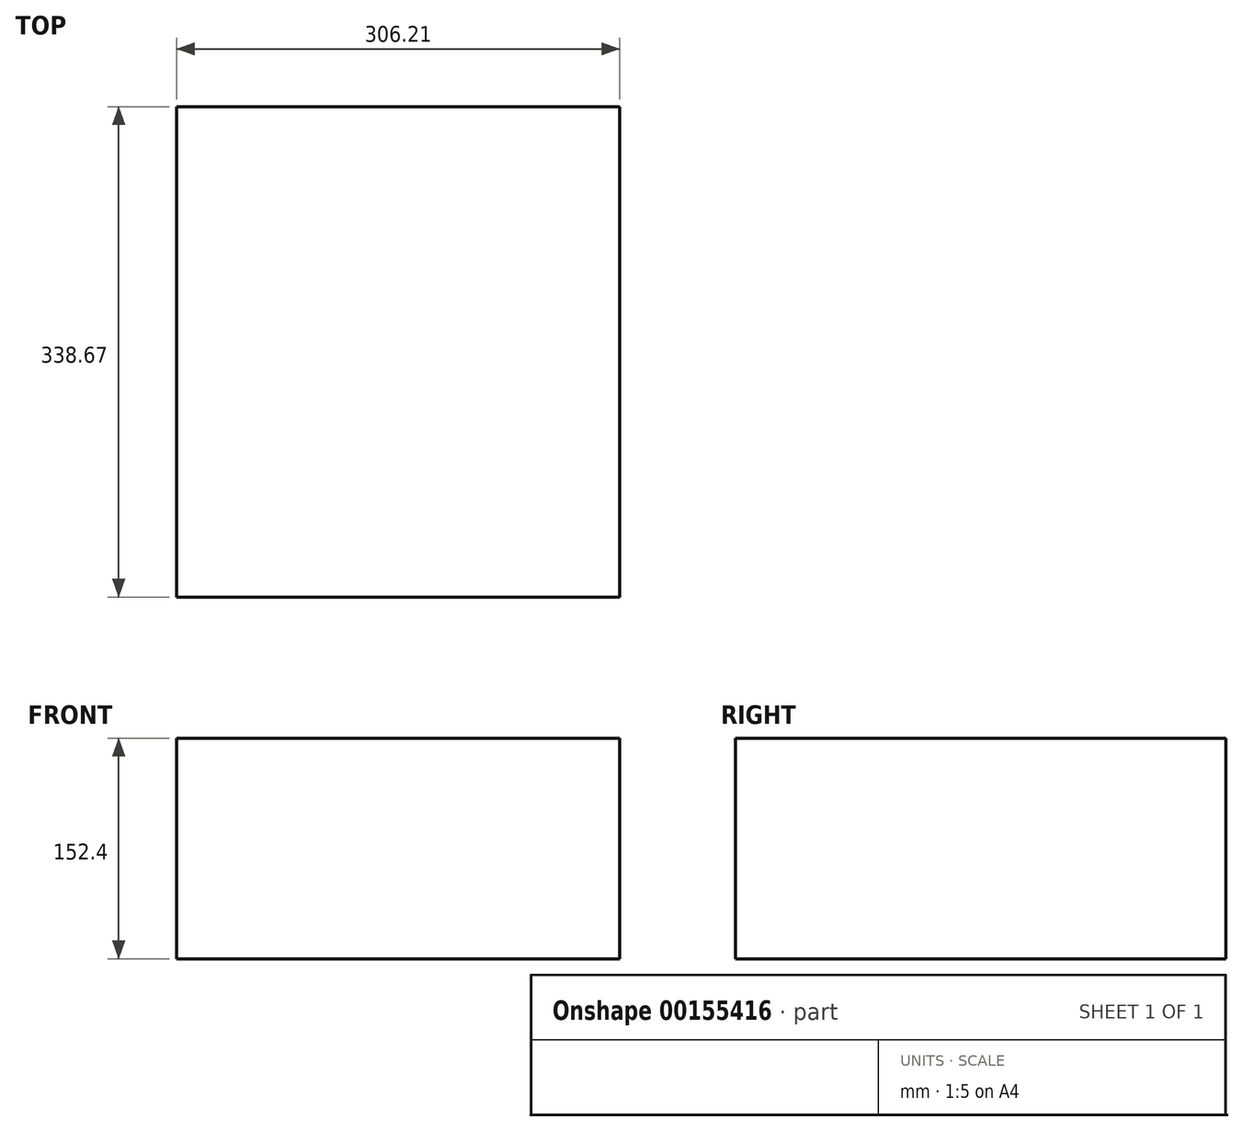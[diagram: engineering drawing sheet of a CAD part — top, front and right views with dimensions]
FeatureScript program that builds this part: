
annotation { "Feature Type Name" : "Feature", "Feature Type Description" : "" }
export const myFeature = defineFeature(function(context is Context, id is Id, definition is map)
    precondition{}
    {
        {
            var Q0;
            Q0=qCreatedBy(makeId("Top.planeOp"),FACE);
            var sketch = newSketch(context, id + "F0", { "sketchPlane" : qUnion([Q0])});
            skLineSegment(sketch, "E0.bottom", {"start": v(-152.4, 168.62) * mm, "end": v(153.81, 168.62) * mm});
            skLineSegment(sketch, "E0.top", {"start": v(-152.4, -170.05) * mm, "end": v(153.81, -170.05) * mm});
            skLineSegment(sketch, "E0.left", {"start": v(-152.4, 168.62) * mm, "end": v(-152.4, -170.05) * mm});
            skLineSegment(sketch, "E0.right", {"start": v(153.81, 168.62) * mm, "end": v(153.81, -170.05) * mm});
            skSolve(sketch);
        }
        {
            var Q0;
            Q0 = qSketchRegion(id + "F0", true);
            extrude(context, id + "F1", {"entities" : qUnion([Q0]), "depth" : 152.4 * mm});
        }
    });
